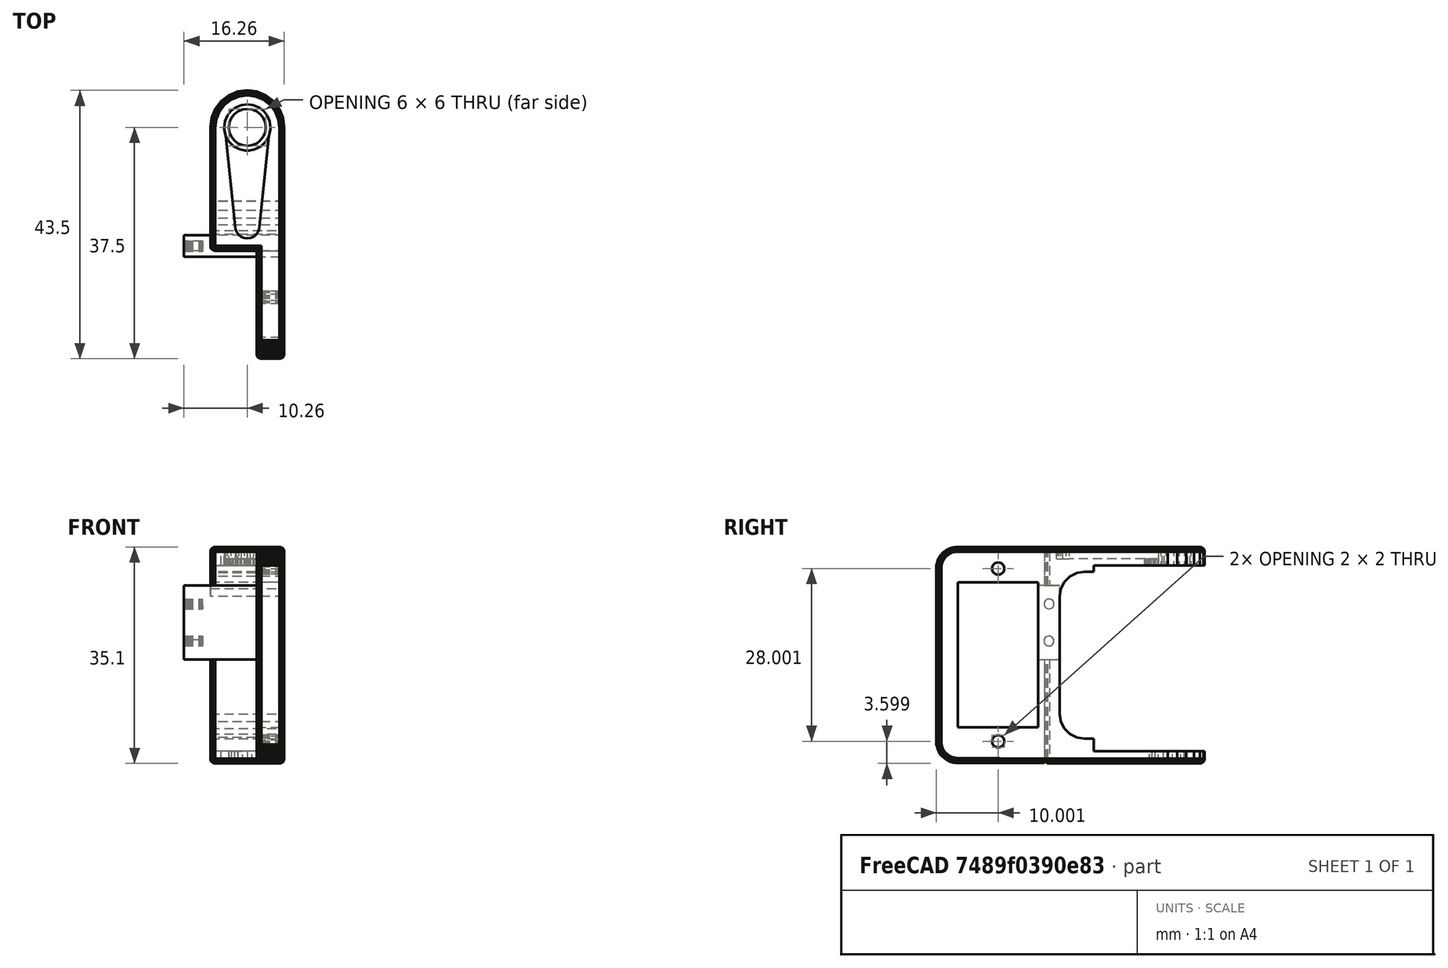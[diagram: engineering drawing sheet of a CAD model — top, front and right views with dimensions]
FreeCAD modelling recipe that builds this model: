
FCSTD DOCUMENT  (FreeCAD 1.0R39319 (Git))
Label: coxa_l_new
License: All rights reserved
LicenseURL: https://en.wikipedia.org/wiki/All_rights_reserved
objects: Mesh::Feature×1, Part::Feature×1, PartDesign::FeatureBase×1, Sketcher::SketchObject×1, PartDesign::Pocket×1, PartDesign::Body×1
note: 9 computed .brp shape members not serialized (recipe doc carries the construction recipe); baked Part::Feature solids carry a one-line shape summary decoded from their .brp

FEATURE [Mesh::Feature] coxa_l  label="mesh1"
FEATURE [Part::Feature] Solid_from_mesh
  shape: bbox 16.47 x 43.71 x 35.31 mm, 2388 faces (baked)
FEATURE [PartDesign::FeatureBase] BaseFeature
  BaseFeature = -> Solid_from_mesh
  Suppressed = false
FEATURE [Sketcher::SketchObject] Sketch
  ArcFitTolerance = 1e-06
  AttachmentOffset = pos=(0,0,170) rot=(0,0,1;0rad)
  AttachmentSupport = -> [YZ_Plane]
  FullyConstrained = false
  MakeInternals = false
  MapMode = 5
  Placement = pos=(170,0,0) rot=(0.57735,0.57735,0.57735;2.0944rad)
  sketch-geometry (8):
    g0: LineSegment StartX=30.4272 StartY=0.819997 StartZ=0 EndX=12.4272 EndY=0.819997 EndZ=0
    g1: LineSegment StartX=12.4272 StartY=0.819997 StartZ=0 EndX=12.4272 EndY=-1.18 EndZ=0
    g2: LineSegment StartX=12.4272 StartY=-1.18 StartZ=0 EndX=30.4272 EndY=-1.18 EndZ=0
    g3: LineSegment StartX=30.4272 StartY=-1.18 StartZ=0 EndX=30.4272 EndY=0.819997 EndZ=0
    g4: LineSegment StartX=30.4117 StartY=27.8941 StartZ=0 EndX=30.4117 EndY=28.8941 EndZ=0
    g5: LineSegment StartX=30.4117 StartY=28.8941 StartZ=0 EndX=12.4117 EndY=28.8941 EndZ=0
    g6: LineSegment StartX=12.4117 StartY=28.8941 StartZ=0 EndX=12.4117 EndY=27.8941 EndZ=0
    g7: LineSegment StartX=12.4117 StartY=27.8941 StartZ=0 EndX=30.4117 EndY=27.8941 EndZ=0
  constraints (20):
    c: Coincident(g0,g1)
    c: Coincident(g1,g2)
    c: Coincident(g2,g3)
    c: Coincident(g3,g0)
    c: Horizontal(g0)
    c: Horizontal(g2)
    c: Vertical(g1)
    c: Vertical(g3)
    c: DistanceX(g0,g0) = 18
    c: DistanceY(g3,g3) = 2
    c: Coincident(g4,g5)
    c: Coincident(g5,g6)
    c: Coincident(g6,g7)
    c: Coincident(g7,g4)
    c: Vertical(g4)
    c: Vertical(g6)
    c: Horizontal(g5)
    c: Horizontal(g7)
    c: DistanceX(g7,g7) = 18
    c: Distance(g4,g4) = 1
FEATURE [PartDesign::Pocket] Pocket
  BaseFeature = -> BaseFeature
  Direction = (-1,0,0)
  Length = 15
  Length2 = 5
  Profile = -> Sketch
  ReferenceAxis = -> Sketch [N_Axis]
  Refine = true
  Suppressed = false
  Type = 0
FEATURE [PartDesign::Body] Body_from_mesh
  AllowCompound = false
  BaseFeature = -> Solid_from_mesh
  Group = -> [BaseFeature,Sketch,Pocket]
  Origin = -> Origin
  Tip = -> Pocket
